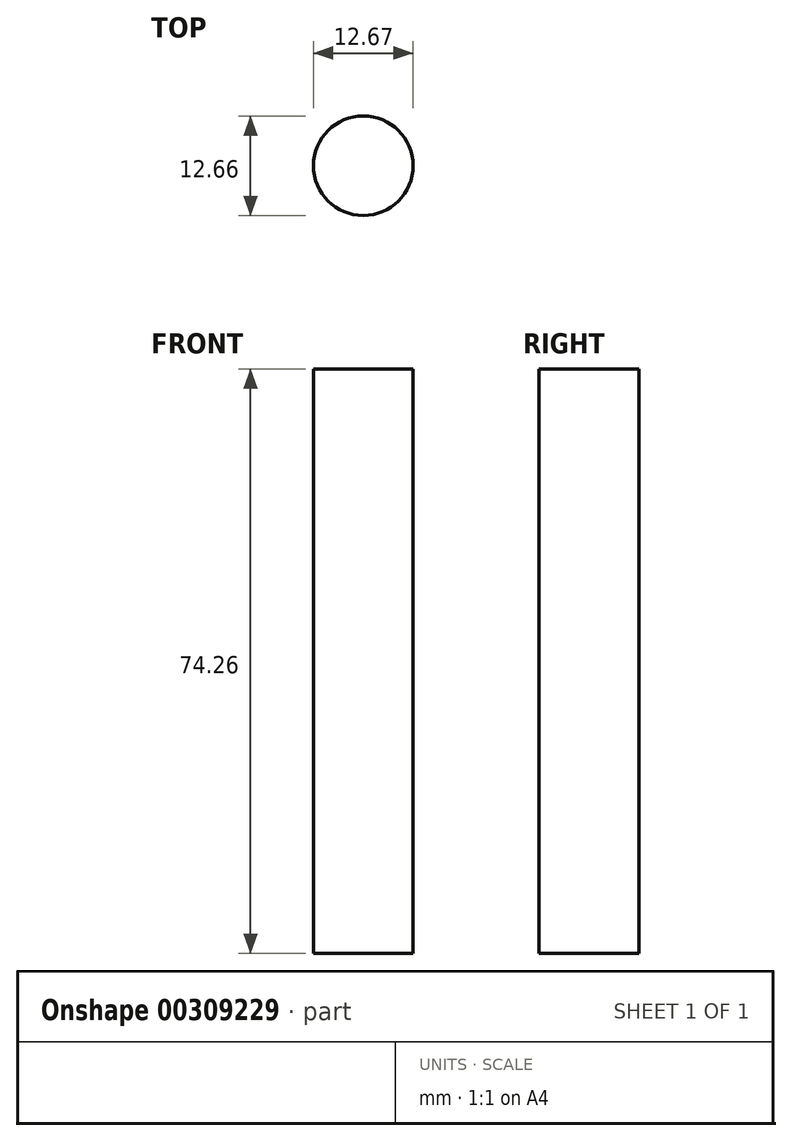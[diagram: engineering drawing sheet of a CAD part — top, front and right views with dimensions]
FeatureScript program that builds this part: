
annotation { "Feature Type Name" : "Feature", "Feature Type Description" : "" }
export const myFeature = defineFeature(function(context is Context, id is Id, definition is map)
    precondition{}
    {
        {
            var Q0;
            Q0=qCreatedBy(makeId("Front.planeOp"),FACE);
            var sketch = newSketch(context, id + "F0", { "sketchPlane" : qUnion([Q0])});
            skLineSegment(sketch, "E0", {"start": v(-9.5, -24.18) * mm, "end": v(-9.5, 50.08) * mm});
            skLineSegment(sketch, "E1", {"start": v(-9.5, 50.08) * mm, "end": v(3.17, 50.08) * mm});
            skLineSegment(sketch, "E2", {"start": v(3.17, 50.08) * mm, "end": v(3.17, -24.18) * mm});
            skLineSegment(sketch, "E3", {"start": v(3.17, -24.18) * mm, "end": v(-9.5, -24.18) * mm});
            skLineSegment(sketch, "E4", {"start": v(-3.17, 50.08) * mm, "end": v(-3.17, -24.18) * mm});
            skSolve(sketch);
        }
        {
            var Q0;
            {var subQ0=sQuery(id+"F0.wireOp",EDGE,"E0");Q0=makeQuery(id+"F0.imprint","IMPRINT",FACE,{"disambiguationData":[TD([[makeQuery(id+"F0.imprint","IMPRINT",EDGE,{"derivedFrom":subQ0}),-1.0]])]});}
            var Q1;
            Q1=sQuery(id+"F0.wireOp",EDGE,"E4");
            revolve(context, id + "F1", {"entities" : qUnion([Q0]), "axis" : qUnion([Q1]), "revolveType" : RevolveType.FULL});
        }
    });
